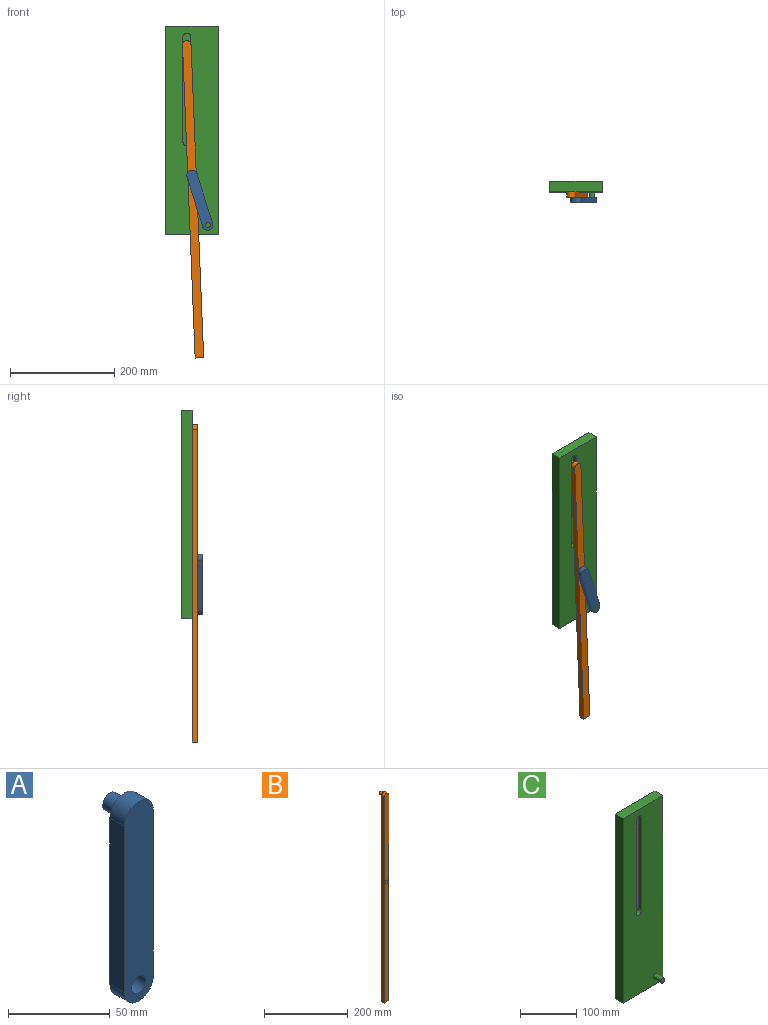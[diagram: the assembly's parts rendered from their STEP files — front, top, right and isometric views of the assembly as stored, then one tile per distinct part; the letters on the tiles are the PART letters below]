
ASSEMBLY  parts=3 mates=3
PART A: 9 faces, bbox 20x20x120 mm
  f0: cylinder r=10mm len=20mm, axis (0,1,0), area 314.2mm2, adj f1,f3,f5,f6
  f1: plane 100x10mm, normal (-1,0,0), area 1000mm2, adj f0,f2,f5,f6
  f2: cylinder r=10mm len=20mm, axis (0,1,0), area 314.2mm2, adj f1,f3,f5,f6
  f3: plane 100x10mm, normal (1,0,0), area 1000mm2, adj f0,f2,f5,f6
  f4: cylinder r=5mm len=10mm, axis (0,1,0), area 314.2mm2, adj f5,f6
  f5: plane 120x20mm, normal (0,-1,0), area 2235.6mm2, adj f0,f1,f2,f3,f4
  f6: plane 120x20mm, normal (0,1,0), area 2157.1mm2, adj f0,f1,f2,f3,f4,f7
  f7: cylinder r=5mm len=10mm, axis (0,-1,0), area 314.2mm2, adj f6,f8
  f8: plane 10x10mm, normal (0,1,0), area 78.5mm2, adj f7
PART B: 9 faces, bbox 16.3x20x608.2 mm
  f0: plane 600x10mm, normal (-1,0,0), area 6000mm2, adj f1,f4,f5,f6
  f1: plane 16.33x10mm, normal (0,0,-1), area 163.3mm2, adj f0,f2,f5,f6
  f2: plane 600x10mm, normal (1,0,0), area 6000mm2, adj f1,f4,f5,f6
  f3: cylinder r=5mm len=10mm, axis (0,1,0), area 314.2mm2, adj f5,f6
  f4: cylinder r=8.17mm len=16.33mm, axis (0,1,0), area 256.5mm2, adj f0,f2,f5,f6
  f5: plane 608.17x16.33mm, normal (0,-1,0), area 9824.6mm2, adj f0,f1,f2,f3,f4
  f6: plane 608.17x16.33mm, normal (0,1,0), area 9746.1mm2, adj f0,f1,f2,f3,f4,f7
  f7: cylinder r=5mm len=10mm, axis (0,-1,0), area 314.2mm2, adj f6,f8
  f8: plane 10x10mm, normal (0,1,0), area 78.5mm2, adj f7
PART C: 15 faces, bbox 100x40x400 mm
  f0: plane 100x20mm, normal (0,0,1), area 2000mm2, adj f1,f7,f8,f11
  f1: plane 400x20mm, normal (-1,0,0), area 8000mm2, adj f0,f2,f8,f11
  f2: plane 100x20mm, normal (0,0,-1), area 2000mm2, adj f1,f7,f8,f11
  f3: cylinder r=7.5mm len=15mm, axis (0,1,0), area 235.6mm2, adj f4,f6,f8,f14
  f4: plane 200x10mm, normal (1,0,0), area 2000mm2, adj f3,f5,f8,f14
  f5: cylinder r=7.5mm len=15mm, axis (0,1,0), area 235.6mm2, adj f4,f6,f8,f14
  f6: plane 200x10mm, normal (-1,0,0), area 2000mm2, adj f3,f5,f8,f14
  f7: plane 400x20mm, normal (1,0,0), area 8000mm2, adj f0,f2,f8,f11
  f8: plane 400x100mm, normal (0,-1,0), area 36744.7mm2, adj f0,f1,f2,f3,f4,f5,f6,f7
  f9: cylinder r=5mm len=20mm, axis (0,1,0), area 628.3mm2, adj f8,f10
  f10: plane 10x10mm, normal (0,-1,0), area 78.5mm2, adj f9
  f11: plane 400x100mm, normal (0,1,0), area 39921.5mm2, adj f0,f1,f2,f7,f12
  f12: cylinder r=5mm len=10mm, axis (0,-1,0), area 314.2mm2, adj f11,f13
  f13: plane 10x10mm, normal (0,1,0), area 78.5mm2, adj f12
  f14: plane 215x15mm, normal (0,-1,0), area 3176.7mm2, adj f3,f4,f5,f6
PLACE A rot(axis=(0,-1,0),17.4deg) t=(-74.28,-20,-288.68)mm
PLACE B rot(axis=(0,-1,0),2.3deg) t=(-141.11,-10,-49.47)mm
PLACE C at identity fixed
MATE revolute B.f3 <-> A.f0  axis (0,1,0) through (-131.04,-10,-299.27)mm
MATE revolute C.f9 <-> A.f2  axis (0,-1,0) through (-101.11,-30,-394.68)mm
MATE pin_slot B.f7 <-> C.f3  axis (0,1,0) through (-141.11,0,-49.47)mm
